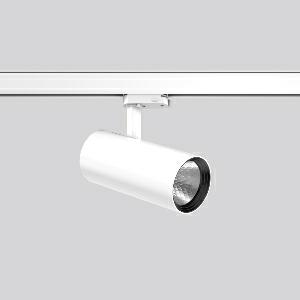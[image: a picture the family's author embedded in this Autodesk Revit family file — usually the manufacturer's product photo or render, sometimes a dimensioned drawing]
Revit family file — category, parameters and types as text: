
# Revit family: deecos_s_mini_742197_002_3_e702
name_source: partatom
category: Lighting Fixtures
units: mm (PartAtom-declared; Revit-internal decimal feet)

## family parameters
Cut with Voids When Loaded = No
Host = Face
Light Source = No
Part Type = Normal
Room Calculation Point = No
Round Connector Dimension = Use Diameter
Shared = No

## types (1)
- DEECOS S mini (1 x LED Modul 935, 2650 lm, 3500)
    Apparent Load = 20 VA
    Approval mark = CE
    CIE Flux Codes = 95 99 100 100 100
    Color Rendering = 92
    Color Temperature = 3500
    Default Elevation = 1800 mm
    Description = Series: DEECOS S mini
LED surface-mounted projector in modern design with no visible cooling ribs. Housing: die-cast aluminium, powder-coated. Rotation range: 356°. Swivel range: 90°. Black plastic ring and recessed LED to prevent glare from the side. Optical assembly with reflector made of MIRO-Silver with 98% total light reflection for outstanding efficiency - can be changed without tools. Best colour rendering index Ra>90. With multi adaptor for 3-circuit tracks 230 V. Suitable for Track on ceiling, Wall track. High quality converter without flickering and stroboscopic effect. The following accessories can be mounted without use of tools: interchangeable lenses, decorative glasses, honeycomb louvre, clear and frosted diffusers, white interchangeable plastic ring. 
Colour: traffic white, matt (RAL 9016)
Diameter: 87 mm
Height: 214 mm
Lamp: LED
Socket: without socket
Colour temperature: 3500K
Colour rendering index (CRI): 92
System power: 20 W
Rated luminous flux: 2650 lm
Luminous efficiency: 133 lm/W
Control gear: Regulated power supply
Protection class: I
Type of protection: IP 20
    Height = 214 mm
    Lamp = 1 x LED Modul 935
    Lamp Light Flux = 2650 lm
    Lamp count = 1
    Length = 87 mm
    Lifetime = 50000 h
    Luminous efficacy = 133 lm/W
    Manufacturer = RZB
    ModVariant = No
    Model = 742197.002.3
    Mounting Place = Ceiling
    Mounting Type = Rail mounted
    Number of Poles = 1
    OnlyDefault = Yes
    Power Factor = 1
    Product Name = DEECOS S mini
    Product group = Track mounted projectors
    ProductGroupID = 301
    Protection Class = Protection class I
    Protection Degree = IP 20
    RLX_Detail_Level = 1
    RLX_Emergency_Light_Flux = 0 lm
    RLX_Emergency_Type = 0
    RLX_Emergency_Type_DB = No
    RlxData = <blob elided: 35565 chars, md5=d8874f39>
    Socket = socket
    Standby Power = 0 W
    System Light Flux = 2650 lm
    System Power = 20 W
    Type Comments = Product without accessories
    Type Image = 741926.002.jpg
    URL = http://relux.com
    VarID = ---
    Voltage = 230 V
    Voltage Range = 220-240 V
    Weight = 0.00 kg
    Width = 0 mm  [stored 0 ft]

note: [stored X ft] marks values corroborated as IEEE doubles in the binary element streams (Revit-internal decimal feet)

## geometry (parser evidence)
native form markers: Blend x4, Sweep x11
no freeform markers — native parametric forms only
